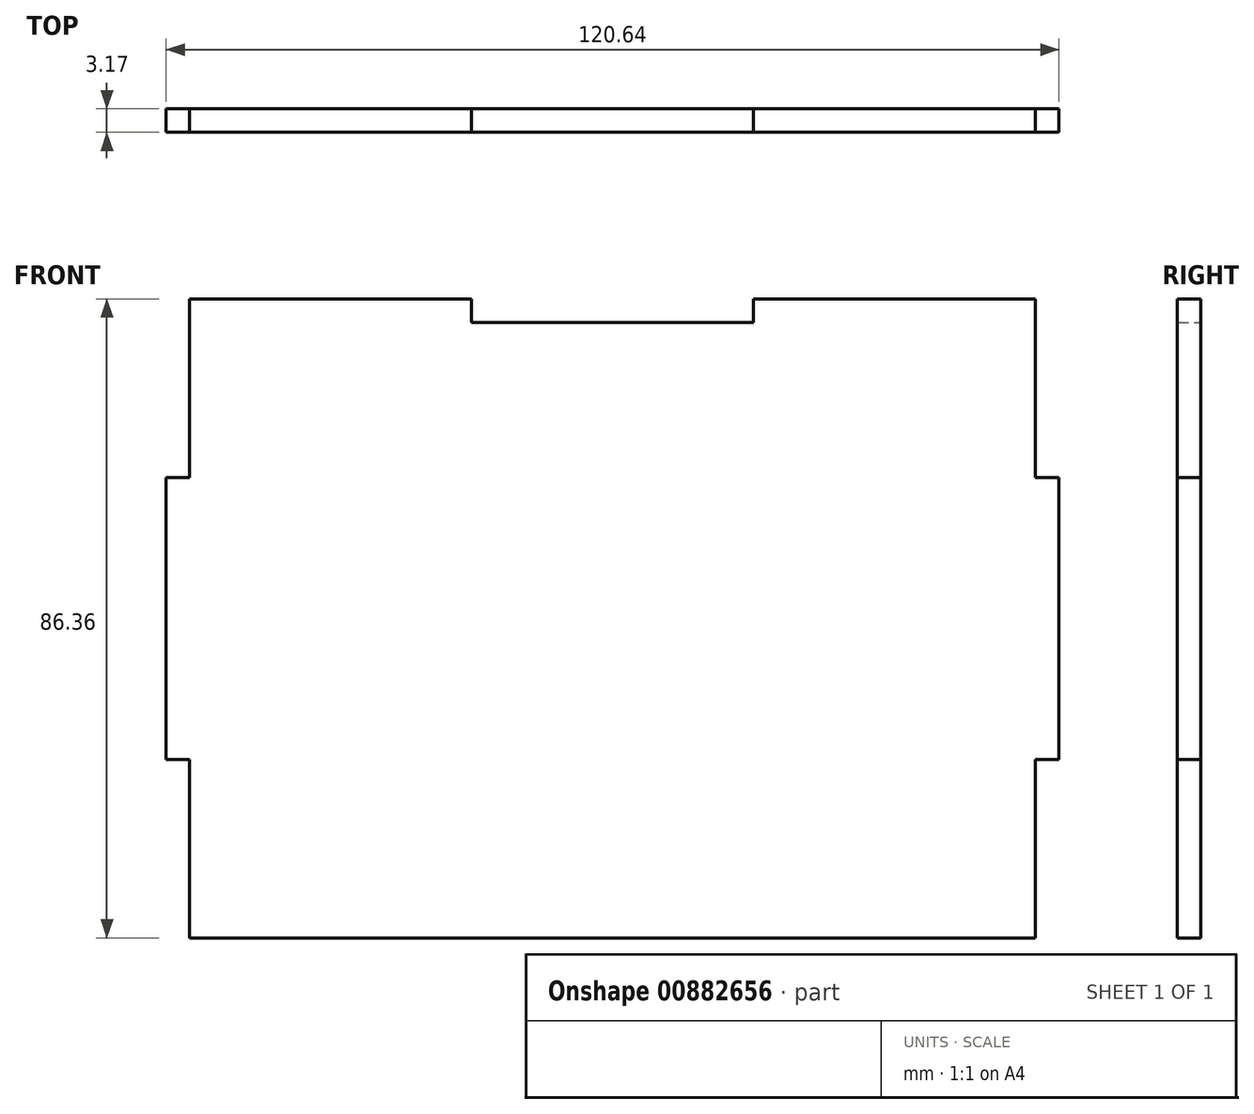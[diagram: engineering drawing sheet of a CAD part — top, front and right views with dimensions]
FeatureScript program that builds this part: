
annotation { "Feature Type Name" : "Feature", "Feature Type Description" : "" }
export const myFeature = defineFeature(function(context is Context, id is Id, definition is map)
    precondition{}
    {
        {
            var Q0;
            Q0=qCreatedBy(makeId("Front.planeOp"),FACE);
            var sketch = newSketch(context, id + "F0", { "sketchPlane" : qUnion([Q0])});
            skLineSegment(sketch, "E0.bottom", {"start": v(60.33, -43.18) * mm, "end": v(-60.33, -43.18) * mm});
            skLineSegment(sketch, "E0.top", {"start": v(60.33, 43.18) * mm, "end": v(-60.33, 43.18) * mm});
            skLineSegment(sketch, "E0.left", {"start": v(60.33, -43.18) * mm, "end": v(60.33, 43.18) * mm});
            skLineSegment(sketch, "E0.right", {"start": v(-60.33, -43.18) * mm, "end": v(-60.33, 43.18) * mm});
            skPoint(sketch, "E0.middle", {"position": v(0, 0) * mm});
            skLineSegment(sketch, "E1", {"start": v(0, 43.18) * mm, "end": v(19.05, 43.18) * mm});
            skLineSegment(sketch, "E2", {"start": v(0, 43.18) * mm, "end": v(-19.05, 43.18) * mm});
            skLineSegment(sketch, "E3", {"start": v(-19.05, 43.18) * mm, "end": v(-19.05, 40) * mm});
            skLineSegment(sketch, "E4", {"start": v(19.05, 43.18) * mm, "end": v(19.05, 40) * mm});
            skLineSegment(sketch, "E5", {"start": v(19.05, 40) * mm, "end": v(-19.05, 40) * mm});
            skLineSegment(sketch, "E6", {"start": v(-60.33, 0) * mm, "end": v(-60.33, 19.05) * mm});
            skLineSegment(sketch, "E7", {"start": v(-60.33, 0) * mm, "end": v(-60.33, -19.05) * mm});
            skLineSegment(sketch, "E8", {"start": v(-60.33, -19.05) * mm, "end": v(-57.15, -19.05) * mm});
            skLineSegment(sketch, "E9", {"start": v(-57.15, -19.05) * mm, "end": v(-57.15, -43.18) * mm});
            skLineSegment(sketch, "E10", {"start": v(-60.33, 19.05) * mm, "end": v(-57.15, 19.05) * mm});
            skLineSegment(sketch, "E11", {"start": v(-57.15, 19.05) * mm, "end": v(-57.15, 43.18) * mm});
            skLineSegment(sketch, "E12.MirrorCS", {"start": v(57.15, 19.05) * mm, "end": v(57.15, 43.18) * mm});
            skLineSegment(sketch, "E13.MirrorCS", {"start": v(57.15, -19.05) * mm, "end": v(57.15, -43.18) * mm});
            skLineSegment(sketch, "E14", {"start": v(57.15, 19.05) * mm, "end": v(60.33, 19.05) * mm});
            skLineSegment(sketch, "E15", {"start": v(57.15, -19.05) * mm, "end": v(60.33, -19.05) * mm});
            skSolve(sketch);
        }
        {
            var Q0;
            {var subQ2=sQuery(id+"F0.wireOp",EDGE,"E3");Q0=makeQuery(id+"F0.imprint","IMPRINT",FACE,{"disambiguationData":[TD([[makeQuery(id+"F0.imprint","IMPRINT",EDGE,{"derivedFrom":subQ2}),-1.0]])]});}
            var Q1;
            Q1=makeQuery(id+"F0.imprint","IMPRINT",FACE,{"disambiguationData":[TD([[makeQuery(id+"F0.imprint","IMPRINT",EDGE,{"derivedFrom":sQuery(id+"F0.wireOp",EDGE,"0iutSNji-cbNv-w4t3-Ue9f-pbIyJnXAomav")}),1.0]])]});
            var Q2;
            {var subQ4=sQuery(id+"F0.wireOp",EDGE,"E4");Q2=makeQuery(id+"F0.imprint","IMPRINT",FACE,{"disambiguationData":[TD([[makeQuery(id+"F0.imprint","IMPRINT",EDGE,{"derivedFrom":subQ4}),1.0]])]});}
            extrude(context, id + "F1", {"entities" : qUnion([Q0, Q1, Q2]), "depth" : 3.17 * mm, "offsetDistance" : 25.4 * mm});
        }
    });
